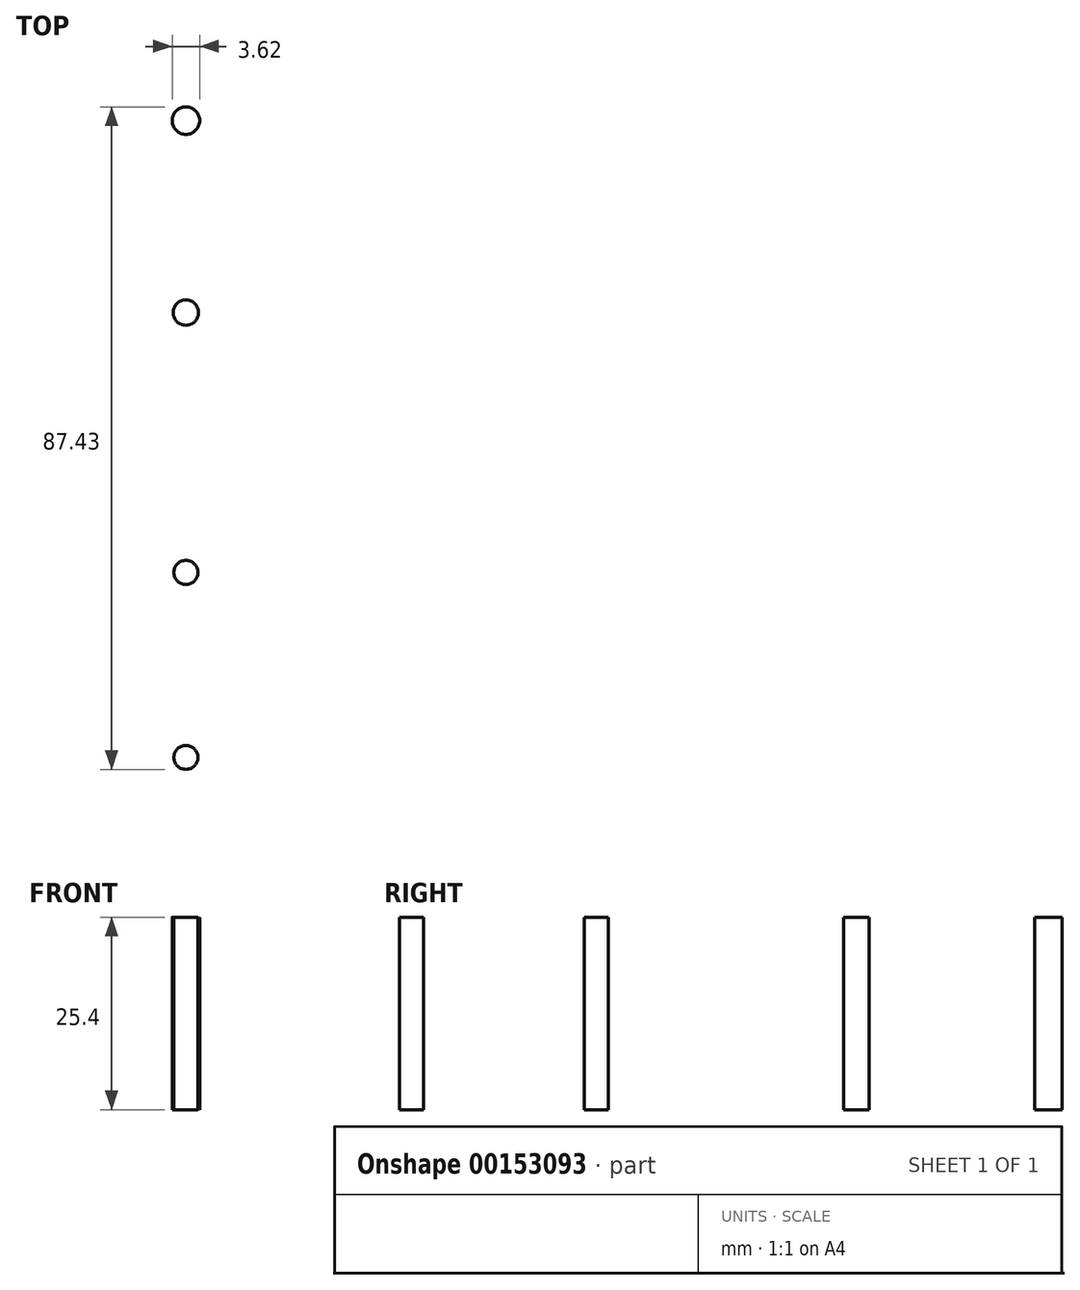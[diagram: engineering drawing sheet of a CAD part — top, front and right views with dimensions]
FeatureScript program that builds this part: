
annotation { "Feature Type Name" : "Feature", "Feature Type Description" : "" }
export const myFeature = defineFeature(function(context is Context, id is Id, definition is map)
    precondition{}
    {
        {
            var Q0;
            Q0=qCreatedBy(makeId("Top.planeOp"),FACE);
            var sketch = newSketch(context, id + "F0", { "sketchPlane" : qUnion([Q0])});
            skLineSegment(sketch, "E0", {"start": v(0, -24.4) * mm, "end": v(0, -19.07) * mm});
            skLineSegment(sketch, "E1", {"start": v(0, -19.07) * mm, "end": v(0, 20.93) * mm});
            skLineSegment(sketch, "E2", {"start": v(0, 0) * mm, "end": v(0, 5.33) * mm});
            skCircle(sketch, "E3", {"center": v(0, -24.4) * mm, "radius": 1.59 * mm});
            skCircle(sketch, "E4", {"center": v(0, 0) * mm, "radius": 1.59 * mm});
            skLineSegment(sketch, "E5", {"start": v(0, 5.33) * mm, "end": v(0, 63.25) * mm});
            skLineSegment(sketch, "E6", {"start": v(0, 5.33) * mm, "end": v(0, 34.3) * mm});
            skCircle(sketch, "E7", {"center": v(0, 34.3) * mm, "radius": 1.68 * mm});
            skLineSegment(sketch, "E8", {"start": v(0, 34.3) * mm, "end": v(0, 39.62) * mm});
            skLineSegment(sketch, "E9", {"start": v(0, 39.62) * mm, "end": v(0, 59.62) * mm});
            skCircle(sketch, "E10", {"center": v(0, 59.62) * mm, "radius": 1.81 * mm});
            skSolve(sketch);
        }
        {
            var Q0;
            Q0 = qSketchRegion(id + "F0", true);
            extrude(context, id + "F1", {"entities" : qUnion([Q0]), "depth" : 25.4 * mm});
        }
    });
